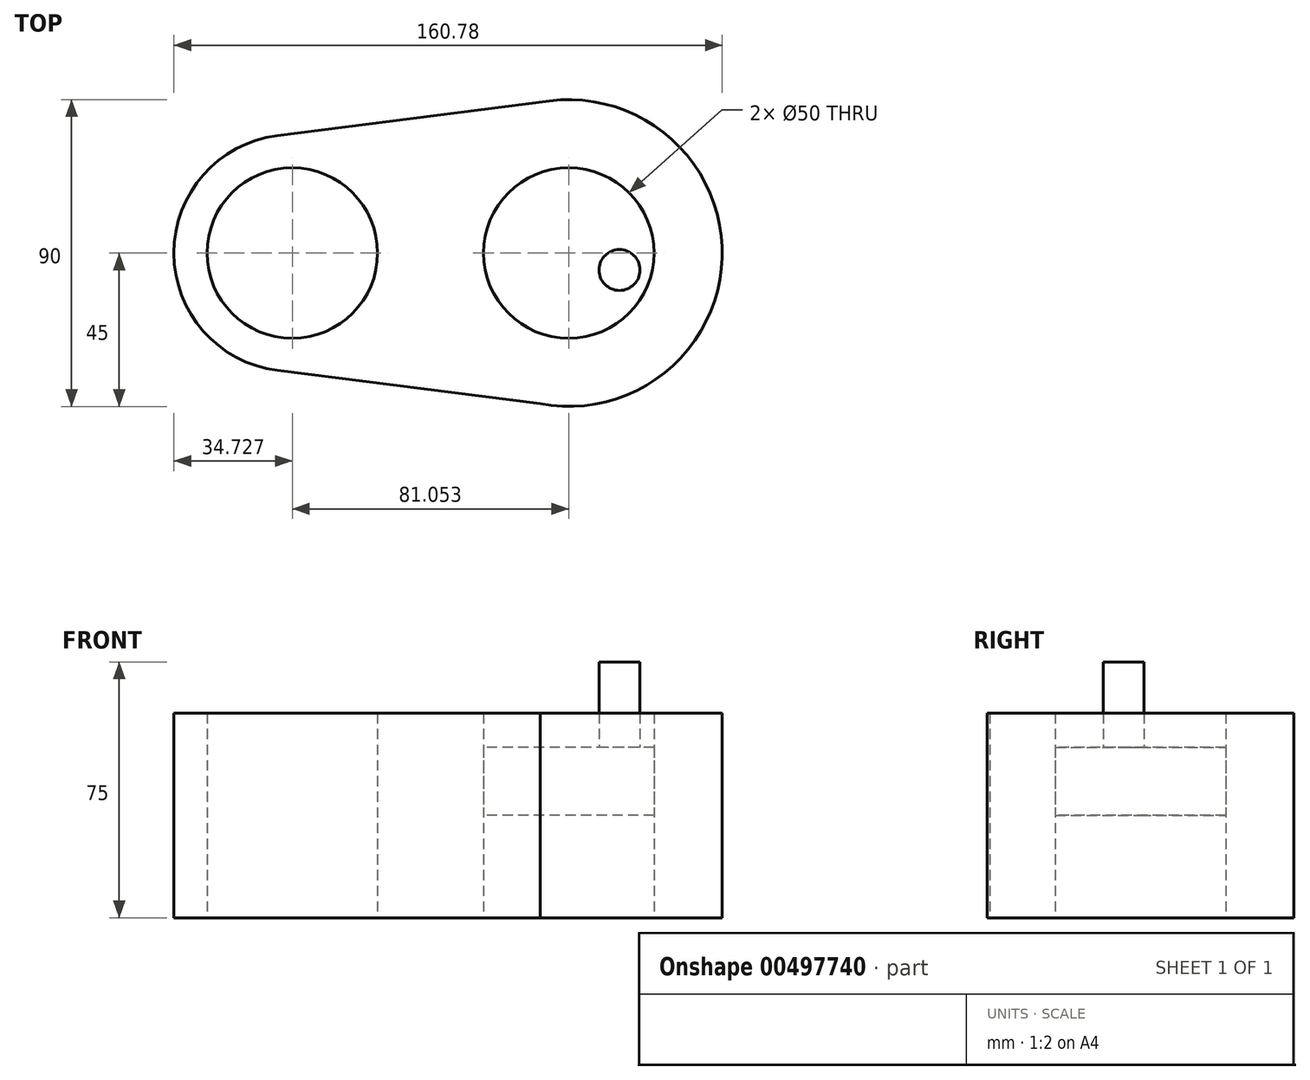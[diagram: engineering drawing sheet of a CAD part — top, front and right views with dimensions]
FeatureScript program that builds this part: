
annotation { "Feature Type Name" : "Feature", "Feature Type Description" : "" }
export const myFeature = defineFeature(function(context is Context, id is Id, definition is map)
    precondition{}
    {
        {
            var Q0;
            Q0=qCreatedBy(makeId("Top.planeOp"),FACE);
            var sketch = newSketch(context, id + "F0", { "sketchPlane" : qUnion([Q0])});
            skCircle(sketch, "E0", {"center": v(0, 0) * mm, "radius": 25 * mm});
            skCircle(sketch, "E1", {"center": v(0, 0) * mm, "radius": 45 * mm});
            skCircle(sketch, "E2", {"center": v(-81.05, 0) * mm, "radius": 25 * mm});
            skCircle(sketch, "E3", {"center": v(-81.05, 0) * mm, "radius": 34.73 * mm});
            skLineSegment(sketch, "E4", {"start": v(-85.45, 34.45) * mm, "end": v(-5.7, 44.64) * mm});
            skLineSegment(sketch, "E5", {"start": v(-85.42, -34.45) * mm, "end": v(-8.42, -44.2) * mm});
            skSolve(sketch);
        }
        {
            var Q0;
            Q0=makeQuery(id+"F0.imprint","IMPRINT",FACE,{"disambiguationData":[TD([[makeQuery(id+"F0.imprint","IMPRINT",EDGE,{"derivedFrom":sQuery(id+"F0.wireOp",EDGE,"E0")}),-1.0]])]});
            var Q1;
            {var subQ0=sQuery(id+"F0.wireOp",EDGE,"E4");Q1=makeQuery(id+"F0.imprint","IMPRINT",FACE,{"disambiguationData":[TD([[makeQuery(id+"F0.imprint","IMPRINT",EDGE,{"derivedFrom":subQ0}),-1.0]])]});}
            var Q2;
            Q2=makeQuery(id+"F0.imprint","IMPRINT",FACE,{"disambiguationData":[TD([[makeQuery(id+"F0.imprint","IMPRINT",EDGE,{"derivedFrom":sQuery(id+"F0.wireOp",EDGE,"E2")}),-1.0]])]});
            extrude(context, id + "F1", {"entities" : qUnion([Q0, Q1, Q2]), "endBound" : BoundingType.SYMMETRIC, "depth" : 60 * mm});
        }
        {
            var Q0;
            Q0=makeQuery(id+"F0.imprint","IMPRINT",FACE,{"disambiguationData":[TD([[makeQuery(id+"F0.imprint","IMPRINT",EDGE,{"derivedFrom":sQuery(id+"F0.wireOp",EDGE,"E0")}),1.0]])]});
            extrude(context, id + "F2", {"entities" : qUnion([Q0]), "depth" : 20 * mm});
        }
        {
            var Q0;
            Q0=makeQuery(id+"F2.opExtrude","CAP_FACE",FACE,{"disambiguationData":[OSD([sQuery(id+"F0.wireOp",EDGE,"E0")])],"isStart":false});
            var sketch = newSketch(context, id + "F3", { "sketchPlane" : qUnion([Q0])});
            skCircle(sketch, "E6", {"center": v(14.89, -4.96) * mm, "radius": 6.01 * mm});
            skSolve(sketch);
        }
        {
            var Q0;
            Q0=makeQuery(id+"F3.imprint","IMPRINT",FACE,{"disambiguationData":[TD([[makeQuery(id+"F3.imprint","IMPRINT",EDGE,{"derivedFrom":sQuery(id+"F3.wireOp",EDGE,"E6")}),1.0]])]});
            extrude(context, id + "F4", {"entities" : qUnion([Q0]), "operationType" : NewBodyOperationType.ADD, "depth" : 25 * mm});
        }
    });
